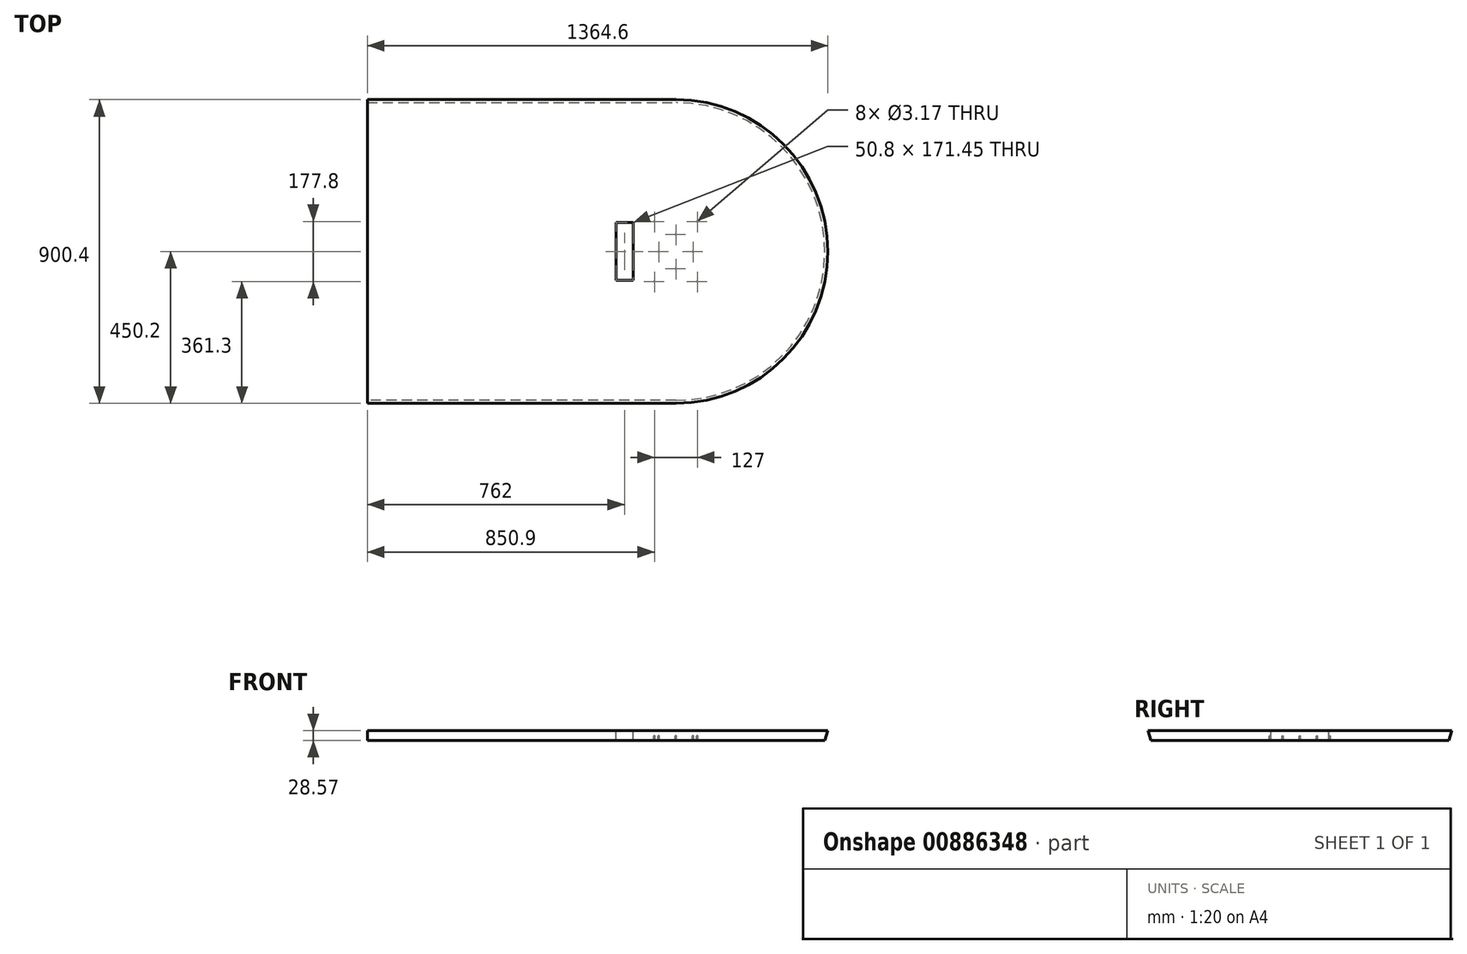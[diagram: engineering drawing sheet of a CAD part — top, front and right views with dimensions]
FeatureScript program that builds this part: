
annotation { "Feature Type Name" : "Feature", "Feature Type Description" : "" }
export const myFeature = defineFeature(function(context is Context, id is Id, definition is map)
    precondition{}
    {
        {
            var Q0;
            Q0=qCreatedBy(makeId("Top.planeOp"),FACE);
            var sketch = newSketch(context, id + "F0", { "sketchPlane" : qUnion([Q0])});
            skLineSegment(sketch, "E0.bottom", {"start": v(-457.2, 457.2) * mm, "end": v(457.2, 457.2) * mm});
            skLineSegment(sketch, "E0.top", {"start": v(-457.2, -457.2) * mm, "end": v(457.2, -457.2) * mm});
            skLineSegment(sketch, "E0.left", {"start": v(-457.2, 457.2) * mm, "end": v(-457.2, -457.2) * mm});
            skLineSegment(sketch, "E0.right", {"start": v(457.2, 457.2) * mm, "end": v(457.2, -457.2) * mm});
            skPoint(sketch, "E0.middle", {"position": v(0, 0) * mm});
            skArc(sketch, "E1", {"start": v(457.2, 457.2) * mm, "mid": v(914.4, 0) * mm, "end": v(457.2, -457.2) * mm});
            skSolve(sketch);
        }
        {
            var Q0;
            Q0=makeQuery(id+"F0.imprint","IMPRINT",FACE,{"disambiguationData":[TD([[makeQuery(id+"F0.imprint","IMPRINT",EDGE,{"derivedFrom":sQuery(id+"F0.wireOp",EDGE,"E0.bottom")}),-1.0]])]});
            var Q1;
            Q1=makeQuery(id+"F0.imprint","IMPRINT",FACE,{"disambiguationData":[TD([[makeQuery(id+"F0.imprint","IMPRINT",EDGE,{"derivedFrom":sQuery(id+"F0.wireOp",EDGE,"E0.right")}),1.0]])]});
            extrude(context, id + "F1", {"entities" : qUnion([Q0, Q1]), "depth" : 28.57 * mm, "offsetDistance" : 25.4 * mm});
        }
        {
            var Q0;
            Q0=makeQuery(id+"F1.opExtrude","CAP_FACE",FACE,{"disambiguationData":[OSD([sQuery(id+"F0.wireOp",EDGE,"E0.bottom"),sQuery(id+"F0.wireOp",EDGE,"E0.top"),sQuery(id+"F0.wireOp",EDGE,"E0.left"),sQuery(id+"F0.wireOp",EDGE,"E1")])],"isStart":false});
            var sketch = newSketch(context, id + "F2", { "sketchPlane" : qUnion([Q0])});
            skLineSegment(sketch, "E2.bottom", {"start": v(533.4, 101.6) * mm, "end": v(381, 101.6) * mm});
            skLineSegment(sketch, "E2.top", {"start": v(533.4, -101.6) * mm, "end": v(381, -101.6) * mm});
            skLineSegment(sketch, "E2.left", {"start": v(533.4, 101.6) * mm, "end": v(533.4, -101.6) * mm});
            skLineSegment(sketch, "E2.right", {"start": v(381, 101.6) * mm, "end": v(381, -101.6) * mm});
            skPoint(sketch, "E2.middle", {"position": v(457.2, 0) * mm});
            skLineSegment(sketch, "E3", {"start": v(381, 0) * mm, "end": v(304.8, 0) * mm});
            skLineSegment(sketch, "E4.bottom", {"start": v(279.4, 85.72) * mm, "end": v(330.2, 85.72) * mm});
            skLineSegment(sketch, "E4.top", {"start": v(279.4, -85.73) * mm, "end": v(330.2, -85.73) * mm});
            skLineSegment(sketch, "E4.left", {"start": v(279.4, 85.72) * mm, "end": v(279.4, -85.73) * mm});
            skLineSegment(sketch, "E4.right", {"start": v(330.2, 85.72) * mm, "end": v(330.2, -85.73) * mm});
            skPoint(sketch, "E4.middle", {"position": v(304.8, 0) * mm});
            skSolve(sketch);
        }
        {
            var Q0;
            {var subQ1=sQuery(id+"F2.wireOp",EDGE,"E4.bottom");Q0=makeQuery(id+"F2.imprint","IMPRINT",FACE,{"disambiguationData":[TD([[makeQuery(id+"F2.imprint","IMPRINT",EDGE,{"derivedFrom":subQ1}),-1.0]])]});}
            extrude(context, id + "F3", {"entities" : qUnion([Q0]), "operationType" : NewBodyOperationType.REMOVE, "oppositeDirection" : true, "depth" : 31.75 * mm, "offsetDistance" : 25.4 * mm});
        }
        {
            var Q0;
            Q0=makeQuery(id+"F1.opExtrude","CAP_FACE",FACE,{"disambiguationData":[OSD([sQuery(id+"F0.wireOp",EDGE,"E0.bottom"),sQuery(id+"F0.wireOp",EDGE,"E0.top"),sQuery(id+"F0.wireOp",EDGE,"E0.left"),sQuery(id+"F0.wireOp",EDGE,"E1")])],"isStart":true});
            var sketch = newSketch(context, id + "F4", { "sketchPlane" : qUnion([Q0])});
            skLineSegment(sketch, "E5.bottom", {"start": v(533.4, 101.6) * mm, "end": v(381, 101.6) * mm});
            skLineSegment(sketch, "E5.top", {"start": v(533.4, -101.6) * mm, "end": v(381, -101.6) * mm});
            skLineSegment(sketch, "E5.left", {"start": v(533.4, 101.6) * mm, "end": v(533.4, -101.6) * mm});
            skLineSegment(sketch, "E5.right", {"start": v(381, 101.6) * mm, "end": v(381, -101.6) * mm});
            skPoint(sketch, "E5.middle", {"position": v(457.2, 0) * mm});
            skLineSegment(sketch, "E6", {"start": v(457.2, 0) * mm, "end": v(457.2, 50.8) * mm});
            skLineSegment(sketch, "E7.bottom", {"start": v(520.7, 88.9) * mm, "end": v(393.7, 88.9) * mm});
            skLineSegment(sketch, "E7.top", {"start": v(520.7, -88.9) * mm, "end": v(393.7, -88.9) * mm});
            skLineSegment(sketch, "E7.left", {"start": v(520.7, 88.9) * mm, "end": v(520.7, -88.9) * mm});
            skLineSegment(sketch, "E7.right", {"start": v(393.7, 88.9) * mm, "end": v(393.7, -88.9) * mm});
            skPoint(sketch, "E8", {"position": v(393.7, 88.9) * mm});
            skPoint(sketch, "E9", {"position": v(520.7, 88.9) * mm});
            skPoint(sketch, "E10", {"position": v(520.7, -88.9) * mm});
            skPoint(sketch, "E11", {"position": v(393.7, -88.9) * mm});
            skPoint(sketch, "E12", {"position": v(457.2, 50.8) * mm});
            skLineSegment(sketch, "E13", {"start": v(457.2, 0) * mm, "end": v(457.2, -50.8) * mm});
            skPoint(sketch, "E14", {"position": v(457.2, -50.8) * mm});
            skLineSegment(sketch, "E15", {"start": v(457.2, 0) * mm, "end": v(508, 0) * mm});
            skLineSegment(sketch, "E16", {"start": v(457.2, 0) * mm, "end": v(406.4, 0) * mm});
            skPoint(sketch, "E17", {"position": v(508, 0) * mm});
            skPoint(sketch, "E18", {"position": v(406.4, 0) * mm});
            skSolve(sketch);
        }
        {
            var Q0;
            Q0=sQuery(id+"F4.wireOp",VERTEX,"E8");
            var Q1;
            Q1=sQuery(id+"F4.wireOp",VERTEX,"E7.bottom.start");
            var Q2;
            Q2=sQuery(id+"F4.wireOp",VERTEX,"E12");
            var Q3;
            Q3=sQuery(id+"F4.wireOp",VERTEX,"E18");
            var Q4;
            Q4=sQuery(id+"F4.wireOp",VERTEX,"E17");
            var Q5;
            Q5=sQuery(id+"F4.wireOp",VERTEX,"E13.end");
            var Q6;
            Q6=sQuery(id+"F4.wireOp",VERTEX,"E11");
            var Q7;
            Q7=sQuery(id+"F4.wireOp",VERTEX,"E7.top.start");
            var Q8;
            Q8=makeQuery(id+"F1.opExtrude","SWEPT_BODY",BODY,{"disambiguationData":[OSD([sQuery(id+"F0.wireOp",EDGE,"E0.bottom"),sQuery(id+"F0.wireOp",EDGE,"E0.top"),sQuery(id+"F0.wireOp",EDGE,"E0.left"),sQuery(id+"F0.wireOp",EDGE,"E1")])]});
            hole(context, id + "F5", {"style" : HoleStyle.SIMPLE, "endStyle" : HoleEndStyle.BLIND, "holeDiameter" : 3.17 * mm, "majorDiameter" : 6.35 * mm, "holeDepth" : 12.7 * mm, "isTappedThrough" : true, "tappedDepth" : 12.7 * mm, "tapClearance" : 3, "locations" : qUnion([Q0, Q1, Q2, Q3, Q4, Q5, Q6, Q7]), "scope" : qUnion([Q8]), "startStyle" : HoleStartStyle.SKETCH});
        }
        {
            var Q0;
            Q0=makeQuery(id+"F1.opExtrude","CAP_EDGE",EDGE,{"disambiguationData":[OSD([sQuery(id+"F0.wireOp",EDGE,"E0.top")])],"isStart":true});
            var Q1;
            Q1=makeQuery(id+"F1.opExtrude","CAP_EDGE",EDGE,{"disambiguationData":[OSD([sQuery(id+"F0.wireOp",EDGE,"E1")])],"isStart":true});
            var Q2;
            Q2=makeQuery(id+"F1.opExtrude","CAP_EDGE",EDGE,{"disambiguationData":[OSD([sQuery(id+"F0.wireOp",EDGE,"E0.bottom")])],"isStart":true});
            chamfer(context, id + "F6", {"entities" : qUnion([Q0, Q1, Q2]), "chamferType" : ChamferType.TWO_OFFSETS, "width1" : 16 * mm, "oppositeDirection" : false, "width2" : 50.8 * mm, "tangentPropagation" : true});
        }
    });
